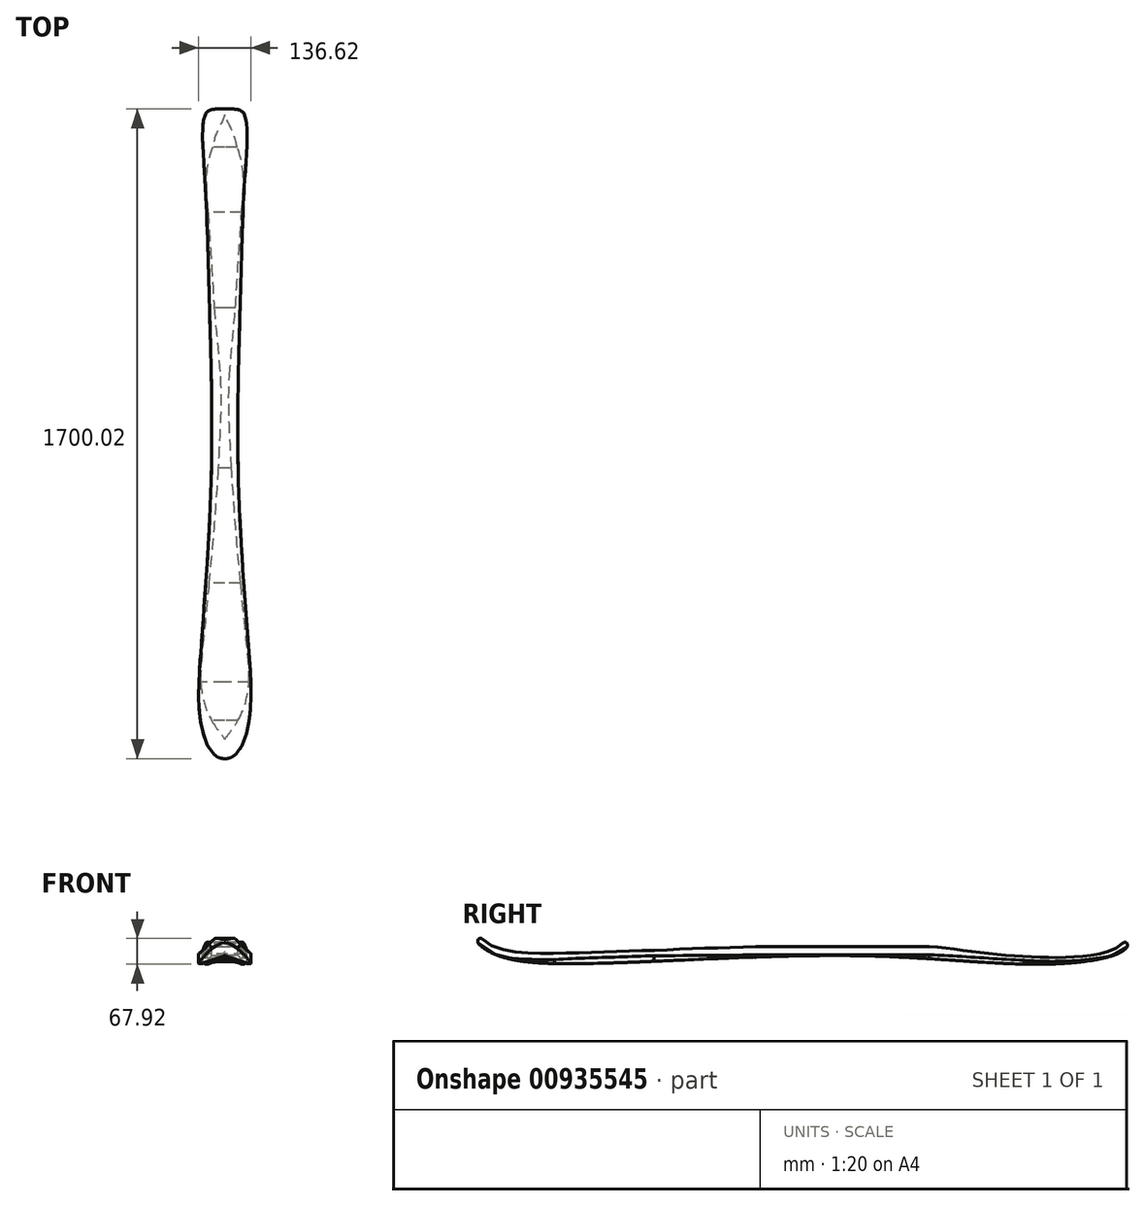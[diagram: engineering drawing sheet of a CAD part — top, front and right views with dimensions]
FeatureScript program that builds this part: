
annotation { "Feature Type Name" : "Feature", "Feature Type Description" : "" }
export const myFeature = defineFeature(function(context is Context, id is Id, definition is map)
    precondition{}
    {
        {
            var Q0;
            Q0=qCreatedBy(makeId("Right.planeOp"),FACE);
            var sketch = newSketch(context, id + "F0", { "sketchPlane" : qUnion([Q0])});
            skLineSegment(sketch, "E0.bottom", {"start": v(-1000, 0) * mm, "end": v(700, 0) * mm, "construction": true});
            skLineSegment(sketch, "E0.top", {"start": v(-1000, -45) * mm, "end": v(700, -45) * mm, "construction": true});
            skLineSegment(sketch, "E0.left", {"start": v(-1000, 0) * mm, "end": v(-1000, -45) * mm, "construction": true});
            skLineSegment(sketch, "E0.right", {"start": v(700, 0) * mm, "end": v(700, -45) * mm, "construction": true});
            skPoint(sketch, "E1.3.internal.snap0", {"position": v(-1000, -22.5) * mm});
            skFitSpline(sketch, "E1", {"points": [v(-1000, 10) * mm, v(-950, -22.5) * mm, v(-760, -45) * mm, v(0, -24) * mm, v(520, -45) * mm, v(700, 0) * mm], "startDerivative": vector(249.3, -384.63) * mm, "endDerivative": vector(259.11, 471.11) * mm});
            skLineSegment(sketch, "E2", {"start": v(-240, 0) * mm, "end": v(180, 0) * mm});
            skArc(sketch, "E3", {"start": v(-988.18, 19.15) * mm, "mid": v(-998.3, 20.01) * mm, "end": v(-1000, 10) * mm});
            skFitSpline(sketch, "E4", {"points": [v(-988.18, 19.15) * mm, v(-760, -17) * mm, v(-520, -9) * mm, v(-240, 0) * mm], "startDerivative": vector(357.43, -389.9) * mm, "endDerivative": vector(510.1, 0) * mm});
            skArc(sketch, "E5", {"start": v(700, 0) * mm, "mid": v(697.77, 9.73) * mm, "end": v(687.85, 8.63) * mm});
            skFitSpline(sketch, "E6", {"points": [v(180, 0) * mm, v(247.5, -6.88) * mm, v(520, -28.75) * mm, v(687.85, 8.63) * mm], "startDerivative": vector(344.95, 0) * mm, "endDerivative": vector(198.08, 220) * mm});
            skSolve(sketch);
        }
        {
            var Q0;
            Q0=qCreatedBy(makeId("Top.planeOp"),FACE);
            var sketch = newSketch(context, id + "F1", { "sketchPlane" : qUnion([Q0])});
            skFitSpline(sketch, "E7", {"points": [v(0, 700) * mm, v(-50, 687.85) * mm, v(-52.5, 520) * mm, v(-40, 180) * mm, v(-35, -240) * mm, v(-60, -680) * mm, v(-60, -920) * mm, v(0, -1000) * mm], "startDerivative": vector(-1236.08, 0) * mm, "endDerivative": vector(1045, 0) * mm});
            skLineSegment(sketch, "E8", {"start": v(0, 700) * mm, "end": v(0, -1000) * mm, "construction": true});
            skFitSpline(sketch, "E9.MirrorCS", {"points": [v(0, 700) * mm, v(50, 687.85) * mm, v(52.5, 520) * mm, v(40, 180) * mm, v(35, -240) * mm, v(60, -680) * mm, v(60, -920) * mm, v(0, -1000) * mm], "startDerivative": vector(1236.08, 0) * mm, "endDerivative": vector(-1045, 0) * mm});
            skLineSegment(sketch, "E10.bottom", {"start": v(-75, 750) * mm, "end": v(75, 750) * mm});
            skLineSegment(sketch, "E10.top", {"start": v(-75, -1050) * mm, "end": v(75, -1050) * mm});
            skLineSegment(sketch, "E10.left", {"start": v(-75, 750) * mm, "end": v(-75, -1050) * mm});
            skLineSegment(sketch, "E10.right", {"start": v(75, 750) * mm, "end": v(75, -1050) * mm});
            skSolve(sketch);
        }
        {
            var Q0;
            Q0=makeQuery(id+"F0.imprint","IMPRINT",FACE,{"disambiguationData":[TD([[makeQuery(id+"F0.imprint","IMPRINT",EDGE,{"derivedFrom":sQuery(id+"F0.wireOp",EDGE,"E1")}),1.0]])]});
            extrude(context, id + "F2", {"entities" : qUnion([Q0]), "endBound" : BoundingType.SYMMETRIC, "depth" : 140 * mm});
        }
        {
            var Q0;
            Q0=makeQuery(id+"F1.imprint","IMPRINT",FACE,{"disambiguationData":[TD([[makeQuery(id+"F1.imprint","IMPRINT",EDGE,{"derivedFrom":sQuery(id+"F1.wireOp",EDGE,"E7")}),-1.0]])]});
            extrude(context, id + "F3", {"entities" : qUnion([Q0]), "operationType" : NewBodyOperationType.REMOVE, "endBound" : BoundingType.SYMMETRIC, "depth" : 100 * mm});
        }
        {
            var Q0;
            Q0=qCreatedBy(makeId("Front.planeOp"),FACE);
            cPlane(context, id + "F4", {"entities" : qUnion([Q0]), "cplaneType" : CPlaneType.OFFSET, "offset" : 240 * mm, "width" : 150 * mm, "height" : 150 * mm});
        }
        {
            var Q0;
            Q0=qCreatedBy(id+"F4.planeOp",FACE);
            cPlane(context, id + "F5", {"entities" : qUnion([Q0]), "cplaneType" : CPlaneType.OFFSET, "offset" : 300 * mm, "width" : 150 * mm, "height" : 150 * mm});
        }
        {
            var Q0;
            Q0=qCreatedBy(id+"F5.planeOp",FACE);
            cPlane(context, id + "F6", {"entities" : qUnion([Q0]), "cplaneType" : CPlaneType.OFFSET, "offset" : 260 * mm, "width" : 150 * mm, "height" : 150 * mm});
        }
        {
            var Q0;
            Q0=qCreatedBy(id+"F6.planeOp",FACE);
            cPlane(context, id + "F7", {"entities" : qUnion([Q0]), "cplaneType" : CPlaneType.OFFSET, "offset" : 100 * mm, "width" : 150 * mm, "height" : 150 * mm});
        }
        {
            var Q0;
            Q0=qCreatedBy(makeId("Front.planeOp"),FACE);
            cPlane(context, id + "F8", {"entities" : qUnion([Q0]), "cplaneType" : CPlaneType.OFFSET, "offset" : 180 * mm, "oppositeDirection" : true, "width" : 150 * mm, "height" : 150 * mm});
        }
        {
            var Q0;
            Q0=qCreatedBy(id+"F8.planeOp",FACE);
            cPlane(context, id + "F9", {"entities" : qUnion([Q0]), "cplaneType" : CPlaneType.OFFSET, "offset" : 250 * mm, "oppositeDirection" : true, "width" : 150 * mm, "height" : 150 * mm});
        }
        {
            var Q0;
            Q0=qCreatedBy(id+"F9.planeOp",FACE);
            cPlane(context, id + "F10", {"entities" : qUnion([Q0]), "cplaneType" : CPlaneType.OFFSET, "offset" : 170 * mm, "oppositeDirection" : true, "width" : 150 * mm, "height" : 150 * mm});
        }
        {
            var Q0;
            Q0=qCreatedBy(id+"F10.planeOp",FACE);
            cPlane(context, id + "F11", {"entities" : qUnion([Q0]), "cplaneType" : CPlaneType.OFFSET, "offset" : 85 * mm, "oppositeDirection" : true, "width" : 150 * mm, "height" : 150 * mm});
        }
        {
            var Q0;
            Q0=qCreatedBy(id+"F7.planeOp",FACE);
            cPlane(context, id + "F12", {"entities" : qUnion([Q0]), "cplaneType" : CPlaneType.OFFSET, "offset" : 50 * mm, "width" : 150 * mm, "height" : 150 * mm});
        }
        {
            var Q0;
            Q0=qCreatedBy(makeId("Top.planeOp"),FACE);
            cPlane(context, id + "F13", {"entities" : qUnion([Q0]), "cplaneType" : CPlaneType.OFFSET, "offset" : 46 * mm, "oppositeDirection" : true, "width" : 150 * mm, "height" : 150 * mm});
        }
        {
            var Q0;
            Q0=qCreatedBy(makeId("Right.planeOp"),FACE);
            var sketch = newSketch(context, id + "F14", { "sketchPlane" : qUnion([Q0])});
            skFitSpline(sketch, "E11", {"points": [v(-950, -22.5) * mm, v(-900, -32.05) * mm, v(-800, -34.02) * mm, v(-760, -32) * mm, v(-540, -24.26) * mm, v(-520, -24) * mm, v(-240, -22) * mm, v(0, -22) * mm, v(180, -22) * mm, v(247.5, -24.88) * mm, v(430, -36.26) * mm, v(520, -38.75) * mm, v(600, -33.38) * mm, v(685, -13.47) * mm], "startDerivative": vector(812.8, -310.38) * mm, "endDerivative": vector(960.2, 551.45) * mm});
            skPoint(sketch, "E12", {"position": v(-900, -14.55) * mm});
            skPoint(sketch, "E13", {"position": v(-800, -18.02) * mm});
            skPoint(sketch, "E14", {"position": v(-540, -9.76) * mm});
            skPoint(sketch, "E15", {"position": v(430, -26.26) * mm});
            skPoint(sketch, "E16", {"position": v(600, -23.38) * mm});
            skLineSegment(sketch, "E17", {"start": v(663.32, -25.92) * mm, "end": v(685, -13.47) * mm, "construction": true});
            skLineSegment(sketch, "E18", {"start": v(-900, -32.05) * mm, "end": v(-900, -32.05) * mm});
            skLineSegment(sketch, "E19", {"start": v(-800, -34.02) * mm, "end": v(-800, -39.05) * mm, "construction": true});
            skLineSegment(sketch, "E20", {"start": v(-540, -24.26) * mm, "end": v(-540, -31.48) * mm, "construction": true});
            skLineSegment(sketch, "E21", {"start": v(-900, -32.05) * mm, "end": v(-900, -35.35) * mm, "construction": true});
            skLineSegment(sketch, "E22", {"start": v(-240, -22) * mm, "end": v(-240, -31.61) * mm, "construction": true});
            skLineSegment(sketch, "E23", {"start": v(0, -22) * mm, "end": v(0, -22) * mm});
            skLineSegment(sketch, "E24", {"start": v(180, -22) * mm, "end": v(180, -38.86) * mm, "construction": true});
            skLineSegment(sketch, "E25", {"start": v(430, -36.26) * mm, "end": v(430, -46.86) * mm, "construction": true});
            skLineSegment(sketch, "E26", {"start": v(600, -33.38) * mm, "end": v(600, -44.7) * mm, "construction": true});
            skLineSegment(sketch, "E27", {"start": v(0, -22) * mm, "end": v(0, -33.93) * mm, "construction": true});
            skSolve(sketch);
        }
        {
            var Q0;
            Q0=qCreatedBy(id+"F13.planeOp",FACE);
            var sketch = newSketch(context, id + "F15", { "sketchPlane" : qUnion([Q0])});
            skFitSpline(sketch, "E28", {"points": [v(0, 700) * mm, v(-50, 687.85) * mm, v(-52.5, 520) * mm, v(-40, 180) * mm, v(-35, -240) * mm, v(-60, -680) * mm, v(-60, -920) * mm, v(0, -1000) * mm], "startDerivative": vector(-1236.08, 0) * mm, "endDerivative": vector(1045, 0) * mm});
            skLineSegment(sketch, "E29", {"start": v(0, 700) * mm, "end": v(0, -1000) * mm, "construction": true});
            skFitSpline(sketch, "E30.MirrorCS", {"points": [v(0, 700) * mm, v(50, 687.85) * mm, v(52.5, 520) * mm, v(40, 180) * mm, v(35, -240) * mm, v(60, -680) * mm, v(60, -920) * mm, v(0, -1000) * mm], "startDerivative": vector(1236.08, 0) * mm, "endDerivative": vector(-1045, 0) * mm});
            skLineSegment(sketch, "E31.bottom", {"start": v(-75, 750) * mm, "end": v(75, 750) * mm});
            skLineSegment(sketch, "E31.top", {"start": v(-75, -1050) * mm, "end": v(75, -1050) * mm});
            skLineSegment(sketch, "E31.left", {"start": v(-75, 750) * mm, "end": v(-75, -1050) * mm});
            skLineSegment(sketch, "E31.right", {"start": v(75, 750) * mm, "end": v(75, -1050) * mm});
            skPoint(sketch, "E32", {"position": v(51.58, -950) * mm});
            skPoint(sketch, "E33", {"position": v(-51.58, -950) * mm});
            skPoint(sketch, "E34", {"position": v(63.62, -900) * mm});
            skPoint(sketch, "E35", {"position": v(-63.62, -900) * mm});
            skPoint(sketch, "E36", {"position": v(-67.82, -800) * mm});
            skPoint(sketch, "E37", {"position": v(67.82, -800) * mm});
            skPoint(sketch, "E38", {"position": v(-49.6, -540) * mm});
            skPoint(sketch, "E39", {"position": v(49.6, -540) * mm});
            skPoint(sketch, "E40", {"position": v(-35.38, 0) * mm});
            skPoint(sketch, "E41", {"position": v(35.38, 0) * mm});
            skPoint(sketch, "E42", {"position": v(-47.76, 430) * mm});
            skPoint(sketch, "E43", {"position": v(47.76, 430) * mm});
            skPoint(sketch, "E44", {"position": v(-57.53, 600) * mm});
            skPoint(sketch, "E45", {"position": v(57.53, 600) * mm});
            skPoint(sketch, "E46", {"position": v(-51.5, 685) * mm});
            skPoint(sketch, "E47", {"position": v(51.5, 685) * mm});
            skSolve(sketch);
        }
        {
            var Q0;
            Q0=qCreatedBy(id+"F12.planeOp",FACE);
            var sketch = newSketch(context, id + "F16", { "sketchPlane" : qUnion([Q0])});
            skArc(sketch, "E48", {"start": v(51.58, -46) * mm, "mid": v(0, -22.5) * mm, "end": v(-51.58, -46) * mm});
            skLineSegment(sketch, "E49", {"start": v(-51.58, -46) * mm, "end": v(51.58, -46) * mm});
            skPoint(sketch, "E50", {"position": v(0, -22.5) * mm});
            skSolve(sketch);
        }
        {
            var Q0;
            Q0=qCreatedBy(id+"F7.planeOp",FACE);
            var sketch = newSketch(context, id + "F17", { "sketchPlane" : qUnion([Q0])});
            skLineSegment(sketch, "E51", {"start": v(-63.62, -46) * mm, "end": v(63.62, -46) * mm});
            skArc(sketch, "E52", {"start": v(63.62, -46) * mm, "mid": v(0, -32.05) * mm, "end": v(-63.62, -46) * mm});
            skSolve(sketch);
        }
        {
            var Q0;
            Q0=qCreatedBy(id+"F6.planeOp",FACE);
            var sketch = newSketch(context, id + "F18", { "sketchPlane" : qUnion([Q0])});
            skLineSegment(sketch, "E53", {"start": v(-67.82, -46) * mm, "end": v(67.82, -46) * mm});
            skArc(sketch, "E54", {"start": v(67.82, -46) * mm, "mid": v(0, -34.02) * mm, "end": v(-67.82, -46) * mm});
            skSolve(sketch);
        }
        {
            var Q0;
            Q0=qCreatedBy(id+"F5.planeOp",FACE);
            var sketch = newSketch(context, id + "F19", { "sketchPlane" : qUnion([Q0])});
            skArc(sketch, "E55", {"start": v(49.6, -46) * mm, "mid": v(0, -24.26) * mm, "end": v(-49.6, -46) * mm});
            skLineSegment(sketch, "E56", {"start": v(-49.6, -46) * mm, "end": v(49.6, -46) * mm});
            skSolve(sketch);
        }
        {
            var Q0;
            Q0=qCreatedBy(id+"F4.planeOp",FACE);
            var sketch = newSketch(context, id + "F20", { "sketchPlane" : qUnion([Q0])});
            skArc(sketch, "E57", {"start": v(35, -46) * mm, "mid": v(0, -22) * mm, "end": v(-35, -46) * mm});
            skLineSegment(sketch, "E58", {"start": v(-35, -46) * mm, "end": v(35, -46) * mm});
            skSolve(sketch);
        }
        {
            var Q0;
            Q0=qCreatedBy(makeId("Front.planeOp"),FACE);
            var sketch = newSketch(context, id + "F21", { "sketchPlane" : qUnion([Q0])});
            skArc(sketch, "E59", {"start": v(35.38, -46) * mm, "mid": v(0, -22) * mm, "end": v(-35.38, -46) * mm});
            skLineSegment(sketch, "E60", {"start": v(-35.38, -46) * mm, "end": v(35.38, -46) * mm});
            skSolve(sketch);
        }
        {
            var Q0;
            Q0=qCreatedBy(id+"F8.planeOp",FACE);
            var sketch = newSketch(context, id + "F22", { "sketchPlane" : qUnion([Q0])});
            skArc(sketch, "E61", {"start": v(40, -46) * mm, "mid": v(0, -22) * mm, "end": v(-40, -46) * mm});
            skLineSegment(sketch, "E62", {"start": v(-40, -46) * mm, "end": v(40, -46) * mm});
            skSolve(sketch);
        }
        {
            var Q0;
            Q0=qCreatedBy(id+"F9.planeOp",FACE);
            var sketch = newSketch(context, id + "F23", { "sketchPlane" : qUnion([Q0])});
            skArc(sketch, "E63", {"start": v(47.76, -48) * mm, "mid": v(0, -36.26) * mm, "end": v(-47.76, -48) * mm});
            skLineSegment(sketch, "E64", {"start": v(-47.76, -48) * mm, "end": v(47.76, -48) * mm});
            skSolve(sketch);
        }
        {
            var Q0;
            Q0=qCreatedBy(id+"F10.planeOp",FACE);
            var sketch = newSketch(context, id + "F24", { "sketchPlane" : qUnion([Q0])});
            skArc(sketch, "E65", {"start": v(57.53, -46) * mm, "mid": v(0, -33.38) * mm, "end": v(-57.53, -46) * mm});
            skLineSegment(sketch, "E66", {"start": v(-57.53, -46) * mm, "end": v(57.53, -46) * mm});
            skSolve(sketch);
        }
        {
            var Q0;
            Q0=qCreatedBy(id+"F11.planeOp",FACE);
            var sketch = newSketch(context, id + "F25", { "sketchPlane" : qUnion([Q0])});
            skArc(sketch, "E67", {"start": v(51.5, -46) * mm, "mid": v(0, -13.47) * mm, "end": v(-51.5, -46) * mm});
            skLineSegment(sketch, "E68", {"start": v(-51.5, -46) * mm, "end": v(51.5, -46) * mm});
            skSolve(sketch);
        }
        {
            var Q1;
            Q1=makeQuery(id+"F16.imprint","IMPRINT",FACE,{"disambiguationData":[TD([[makeQuery(id+"F16.imprint","IMPRINT",EDGE,{"derivedFrom":sQuery(id+"F16.wireOp",EDGE,"E48")}),1.0]])]});
            var Q2;
            Q2=makeQuery(id+"F17.imprint","IMPRINT",FACE,{"disambiguationData":[TD([[makeQuery(id+"F17.imprint","IMPRINT",EDGE,{"derivedFrom":sQuery(id+"F17.wireOp",EDGE,"E51")}),1.0]])]});
            var Q3;
            Q3=sQuery(id+"F14.wireOp",EDGE,"E11");
            loft(context, id + "F26", {"operationType" : NewBodyOperationType.REMOVE, "addGuides" : true, "sheetProfilesArray" : [{ "sheetProfileEntities" : qUnion([Q1]) }, { "sheetProfileEntities" : qUnion([Q2]) }], "guidesArray" : [{ "guideEntities" : qUnion([Q3]), "guideDerivativeType" : LoftGuideDerivativeType.DEFAULT, "guideDerivativeMagnitude" : 1 }]});
        }
        {
            var Q1;
            Q1=makeQuery(id+"F17.imprint","IMPRINT",FACE,{"disambiguationData":[TD([[makeQuery(id+"F17.imprint","IMPRINT",EDGE,{"derivedFrom":sQuery(id+"F17.wireOp",EDGE,"E51")}),1.0]])]});
            var Q2;
            Q2=qSketchRegion(id+"F18",true);
            var Q3;
            Q3=sQuery(id+"F14.wireOp",EDGE,"E11");
            loft(context, id + "F27", {"operationType" : NewBodyOperationType.REMOVE, "addGuides" : true, "sheetProfilesArray" : [{ "sheetProfileEntities" : qUnion([Q1]) }, { "sheetProfileEntities" : qUnion([Q2]) }], "guidesArray" : [{ "guideEntities" : qUnion([Q3]), "guideDerivativeType" : LoftGuideDerivativeType.DEFAULT, "guideDerivativeMagnitude" : 1 }]});
        }
        {
            var Q1;
            Q1=qSketchRegion(id+"F18",true);
            var Q2;
            Q2=qSketchRegion(id+"F19",true);
            var Q3;
            Q3=sQuery(id+"F14.wireOp",EDGE,"E11");
            loft(context, id + "F28", {"operationType" : NewBodyOperationType.REMOVE, "addGuides" : true, "sheetProfilesArray" : [{ "sheetProfileEntities" : qUnion([Q1]) }, { "sheetProfileEntities" : qUnion([Q2]) }], "guidesArray" : [{ "guideEntities" : qUnion([Q3]), "guideDerivativeType" : LoftGuideDerivativeType.DEFAULT, "guideDerivativeMagnitude" : 1 }]});
        }
        {
            var Q1;
            Q1=qSketchRegion(id+"F19",true);
            var Q2;
            Q2=qSketchRegion(id+"F20",true);
            var Q3;
            Q3=sQuery(id+"F14.wireOp",EDGE,"E11");
            loft(context, id + "F29", {"operationType" : NewBodyOperationType.REMOVE, "addGuides" : true, "sheetProfilesArray" : [{ "sheetProfileEntities" : qUnion([Q1]) }, { "sheetProfileEntities" : qUnion([Q2]) }], "guidesArray" : [{ "guideEntities" : qUnion([Q3]), "guideDerivativeType" : LoftGuideDerivativeType.DEFAULT, "guideDerivativeMagnitude" : 1 }]});
        }
        {
            var Q1;
            Q1=qSketchRegion(id+"F20",true);
            var Q2;
            Q2=qSketchRegion(id+"F21",true);
            var Q3;
            Q3=sQuery(id+"F14.wireOp",EDGE,"E11");
            loft(context, id + "F30", {"operationType" : NewBodyOperationType.REMOVE, "addGuides" : true, "sheetProfilesArray" : [{ "sheetProfileEntities" : qUnion([Q1]) }, { "sheetProfileEntities" : qUnion([Q2]) }], "guidesArray" : [{ "guideEntities" : qUnion([Q3]), "guideDerivativeType" : LoftGuideDerivativeType.DEFAULT, "guideDerivativeMagnitude" : 1 }]});
        }
        {
            var Q1;
            Q1=makeQuery(id+"F21.imprint","IMPRINT",FACE,{"disambiguationData":[TD([[makeQuery(id+"F21.imprint","IMPRINT",EDGE,{"derivedFrom":sQuery(id+"F21.wireOp",EDGE,"E59")}),1.0]])]});
            var Q2;
            Q2=makeQuery(id+"F22.imprint","IMPRINT",FACE,{"disambiguationData":[TD([[makeQuery(id+"F22.imprint","IMPRINT",EDGE,{"derivedFrom":sQuery(id+"F22.wireOp",EDGE,"E61")}),1.0]])]});
            var Q3;
            Q3=sQuery(id+"F14.wireOp",EDGE,"E11");
            loft(context, id + "F31", {"operationType" : NewBodyOperationType.REMOVE, "addGuides" : true, "sheetProfilesArray" : [{ "sheetProfileEntities" : qUnion([Q1]) }, { "sheetProfileEntities" : qUnion([Q2]) }], "guidesArray" : [{ "guideEntities" : qUnion([Q3]), "guideDerivativeType" : LoftGuideDerivativeType.DEFAULT, "guideDerivativeMagnitude" : 1 }]});
        }
        {
            var Q1;
            Q1=makeQuery(id+"F22.imprint","IMPRINT",FACE,{"disambiguationData":[TD([[makeQuery(id+"F22.imprint","IMPRINT",EDGE,{"derivedFrom":sQuery(id+"F22.wireOp",EDGE,"E61")}),1.0]])]});
            var Q2;
            Q2=qSketchRegion(id+"F23",true);
            var Q3;
            Q3=sQuery(id+"F14.wireOp",EDGE,"E11");
            loft(context, id + "F32", {"operationType" : NewBodyOperationType.REMOVE, "addGuides" : true, "sheetProfilesArray" : [{ "sheetProfileEntities" : qUnion([Q1]) }, { "sheetProfileEntities" : qUnion([Q2]) }], "guidesArray" : [{ "guideEntities" : qUnion([Q3]), "guideDerivativeType" : LoftGuideDerivativeType.DEFAULT, "guideDerivativeMagnitude" : 1 }]});
        }
        {
            var Q1;
            Q1=qSketchRegion(id+"F23",true);
            var Q2;
            Q2=qSketchRegion(id+"F24",true);
            var Q3;
            Q3=sQuery(id+"F14.wireOp",EDGE,"E11");
            loft(context, id + "F33", {"operationType" : NewBodyOperationType.REMOVE, "addGuides" : true, "sheetProfilesArray" : [{ "sheetProfileEntities" : qUnion([Q1]) }, { "sheetProfileEntities" : qUnion([Q2]) }], "guidesArray" : [{ "guideEntities" : qUnion([Q3]), "guideDerivativeType" : LoftGuideDerivativeType.DEFAULT, "guideDerivativeMagnitude" : 1 }]});
        }
        {
            var Q1;
            Q1=makeQuery(id+"F24.imprint","IMPRINT",FACE,{"disambiguationData":[TD([[makeQuery(id+"F24.imprint","IMPRINT",EDGE,{"derivedFrom":sQuery(id+"F24.wireOp",EDGE,"E65")}),1.0]])]});
            var Q2;
            Q2=makeQuery(id+"F25.imprint","IMPRINT",FACE,{"disambiguationData":[TD([[makeQuery(id+"F25.imprint","IMPRINT",EDGE,{"derivedFrom":sQuery(id+"F25.wireOp",EDGE,"E67")}),1.0]])]});
            var Q3;
            Q3=sQuery(id+"F14.wireOp",EDGE,"E11");
            loft(context, id + "F34", {"operationType" : NewBodyOperationType.REMOVE, "addGuides" : true, "sheetProfilesArray" : [{ "sheetProfileEntities" : qUnion([Q1]) }, { "sheetProfileEntities" : qUnion([Q2]) }], "guidesArray" : [{ "guideEntities" : qUnion([Q3]), "guideDerivativeType" : LoftGuideDerivativeType.DEFAULT, "guideDerivativeMagnitude" : 1 }]});
        }
    });
